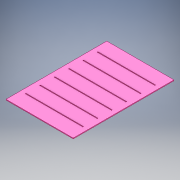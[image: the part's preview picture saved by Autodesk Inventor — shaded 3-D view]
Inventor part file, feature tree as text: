
AUTODESK INVENTOR PART (.ipt)
format: ipt  version: 2018 (Build 220112000, 112)  size: 132,608 bytes
history: native  units: mm
features: extrude x2, sketch x2
ambient origin geometry x8: Origin, YZ Plane, XZ Plane, XY Plane, X Axis, Y Axis, Z Axis, Center Point
bodies: Solid1 (feature_tree)
feature tree (4):
  extrude  "Extrusion1"  Depth=2100.0mm
  extrude  "Extrusion2"  Depth=1400.0mm
  sketch  "Sketch1"  dims[d0=1400.0mm d1=2100.0mm]
  sketch  "Sketch2"  dims[d2=16.0mm d3=0.0mm d4=1400.0mm d5=100.0mm d6=300.0mm d7=1200.0mm d8=16.0mm d9=16.0mm d10=0.0mm d11=60.0mm d13=300.0mm d14=10.0mm d16=10.0mm]
